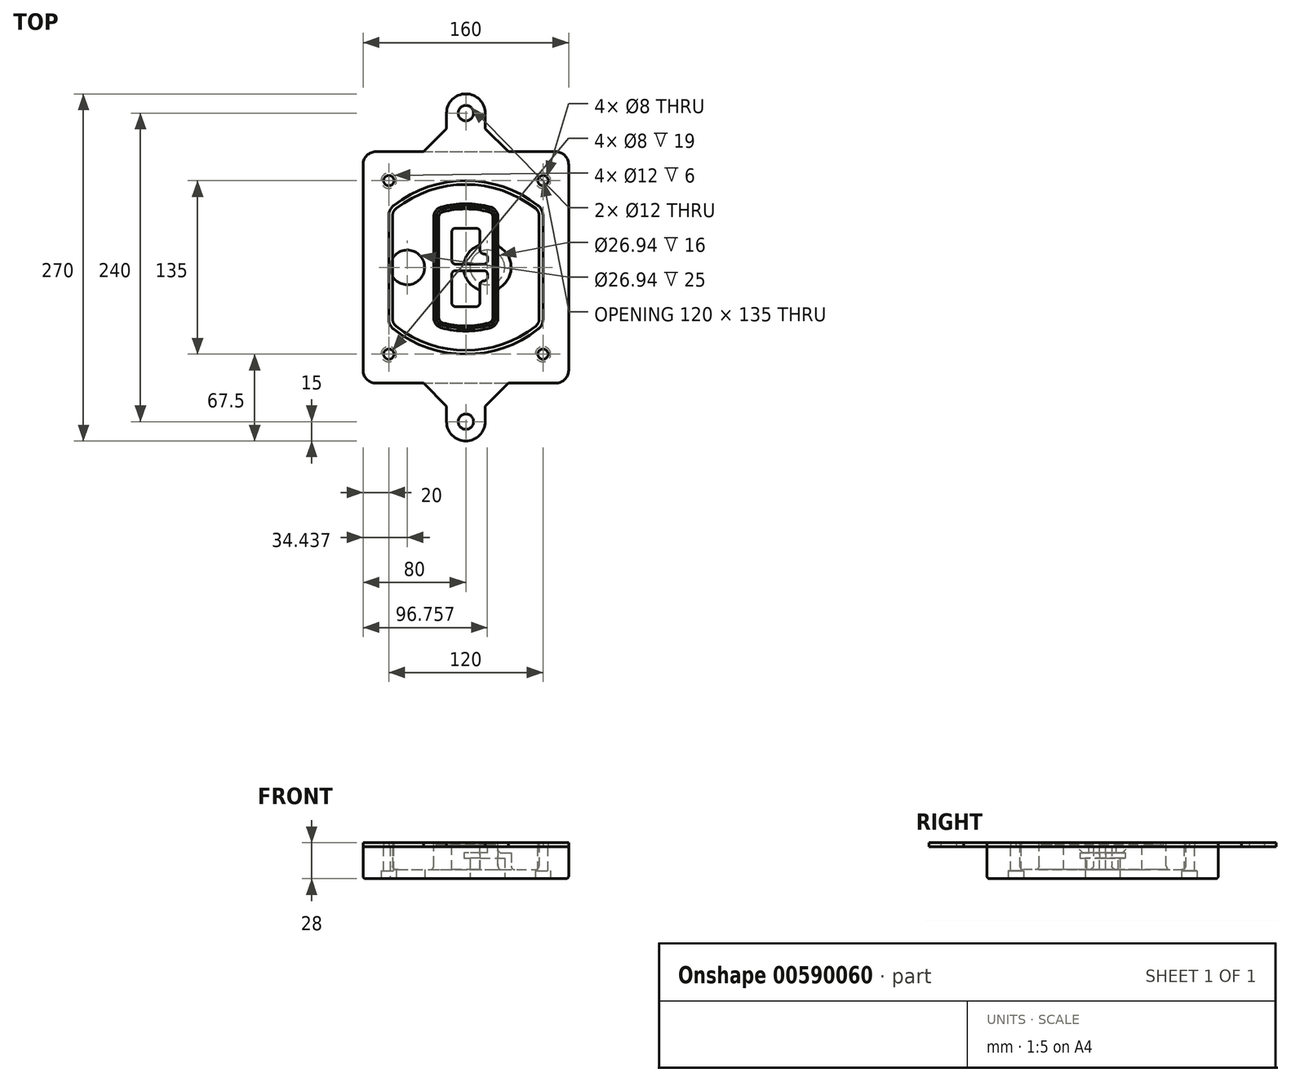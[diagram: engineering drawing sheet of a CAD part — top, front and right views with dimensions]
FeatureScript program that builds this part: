
annotation { "Feature Type Name" : "Feature", "Feature Type Description" : "" }
export const myFeature = defineFeature(function(context is Context, id is Id, definition is map)
    precondition{}
    {
        {
            var Q0;
            Q0=qCreatedBy(makeId("Top.planeOp"),FACE);
            var sketch = newSketch(context, id + "F0", { "sketchPlane" : qUnion([Q0])});
            skPoint(sketch, "E0.rect.middle", {"position": v(0, 0) * mm});
            skLineSegment(sketch, "E1.bottom", {"start": v(-70, -90) * mm, "end": v(70, -90) * mm});
            skLineSegment(sketch, "E1.top", {"start": v(-70, 90) * mm, "end": v(70, 90) * mm});
            skLineSegment(sketch, "E1.left", {"start": v(-80, -80) * mm, "end": v(-80, 80) * mm});
            skLineSegment(sketch, "E1.right", {"start": v(80, -80) * mm, "end": v(80, 80) * mm});
            skLineSegment(sketch, "E2", {"start": v(-80, 90) * mm, "end": v(80, -90) * mm, "construction": true});
            skLineSegment(sketch, "E3", {"start": v(80, 90) * mm, "end": v(-80, -90) * mm, "construction": true});
            skCircle(sketch, "E4", {"center": v(-60, 67.5) * mm, "radius": 4 * mm});
            skCircle(sketch, "E5", {"center": v(60, 67.5) * mm, "radius": 4 * mm});
            skCircle(sketch, "E6", {"center": v(60, -67.5) * mm, "radius": 4 * mm});
            skCircle(sketch, "E7", {"center": v(-60, -67.5) * mm, "radius": 4 * mm});
            skLineSegment(sketch, "E8", {"start": v(-60, 67.5) * mm, "end": v(60, 67.5) * mm, "construction": true});
            skLineSegment(sketch, "E9", {"start": v(60, 67.5) * mm, "end": v(60, -67.5) * mm, "construction": true});
            skLineSegment(sketch, "E10", {"start": v(60, -67.5) * mm, "end": v(-60, -67.5) * mm, "construction": true});
            skLineSegment(sketch, "E11", {"start": v(-60, -67.5) * mm, "end": v(-60, 67.5) * mm, "construction": true});
            skLineSegment(sketch, "E12", {"start": v(-60, 40.3) * mm, "end": v(-60, -40.3) * mm});
            skLineSegment(sketch, "E13", {"start": v(60, 40.3) * mm, "end": v(60, -40.3) * mm});
            skArc(sketch, "E14", {"start": v(56.15, 48.18) * mm, "mid": v(0, 67.5) * mm, "end": v(-56.15, 48.18) * mm});
            skArc(sketch, "E15", {"start": v(-56.15, -48.18) * mm, "mid": v(0, -67.5) * mm, "end": v(56.15, -48.18) * mm});
            skLineSegment(sketch, "E16", {"start": v(-60, 0) * mm, "end": v(60, 0) * mm, "construction": true});
            skPoint(sketch, "E17.visualSharp", {"position": v(-60, -45) * mm});
            skArc(sketch, "E17.filletArc", {"start": v(-60, -40.3) * mm, "mid": v(-58.99, -44.68) * mm, "end": v(-56.15, -48.18) * mm});
            skPoint(sketch, "E18.visualSharp", {"position": v(-60, 45) * mm});
            skArc(sketch, "E18.filletArc", {"start": v(-56.15, 48.18) * mm, "mid": v(-58.99, 44.68) * mm, "end": v(-60, 40.3) * mm});
            skPoint(sketch, "E19.visualSharp", {"position": v(60, 45) * mm});
            skArc(sketch, "E19.filletArc", {"start": v(60, 40.3) * mm, "mid": v(58.99, 44.68) * mm, "end": v(56.15, 48.18) * mm});
            skPoint(sketch, "E20.visualSharp", {"position": v(60, -45) * mm});
            skArc(sketch, "E20.filletArc", {"start": v(56.15, -48.18) * mm, "mid": v(58.99, -44.68) * mm, "end": v(60, -40.3) * mm});
            skPoint(sketch, "E21.visualSharp", {"position": v(-80, 90) * mm});
            skArc(sketch, "E21.filletArc", {"start": v(-70, 90) * mm, "mid": v(-77.07, 87.07) * mm, "end": v(-80, 80) * mm});
            skPoint(sketch, "E22.visualSharp", {"position": v(80, 90) * mm});
            skArc(sketch, "E22.filletArc", {"start": v(80, 80) * mm, "mid": v(77.07, 87.07) * mm, "end": v(70, 90) * mm});
            skPoint(sketch, "E23.visualSharp", {"position": v(80, -90) * mm});
            skArc(sketch, "E23.filletArc", {"start": v(70, -90) * mm, "mid": v(77.07, -87.07) * mm, "end": v(80, -80) * mm});
            skPoint(sketch, "E24.visualSharp", {"position": v(-80, -90) * mm});
            skArc(sketch, "E24.filletArc", {"start": v(-80, -80) * mm, "mid": v(-77.07, -87.07) * mm, "end": v(-70, -90) * mm});
            skArc(sketch, "E25.0", {"start": v(57, 40.3) * mm, "mid": v(56.3, 43.36) * mm, "end": v(54.3, 45.81) * mm});
            skLineSegment(sketch, "E25.1", {"start": v(57, 40.3) * mm, "end": v(57, -40.3) * mm});
            skArc(sketch, "E25.2", {"start": v(54.3, -45.81) * mm, "mid": v(56.3, -43.36) * mm, "end": v(57, -40.3) * mm});
            skArc(sketch, "E25.3", {"start": v(-54.3, -45.81) * mm, "mid": v(0, -64.5) * mm, "end": v(54.3, -45.81) * mm});
            skArc(sketch, "E25.4", {"start": v(-57, -40.3) * mm, "mid": v(-56.3, -43.36) * mm, "end": v(-54.3, -45.81) * mm});
            skArc(sketch, "E25.5", {"start": v(54.3, 45.81) * mm, "mid": v(0, 64.5) * mm, "end": v(-54.3, 45.81) * mm});
            skLineSegment(sketch, "E25.6", {"start": v(-57, 40.3) * mm, "end": v(-57, -40.3) * mm});
            skArc(sketch, "E25.7", {"start": v(-54.3, 45.81) * mm, "mid": v(-56.3, 43.36) * mm, "end": v(-57, 40.3) * mm});
            skArc(sketch, "E26.0", {"start": v(-58.62, 51.33) * mm, "mid": v(-62.58, 46.43) * mm, "end": v(-64, 40.3) * mm});
            skArc(sketch, "E26.1", {"start": v(58.62, 51.33) * mm, "mid": v(0, 71.5) * mm, "end": v(-58.62, 51.33) * mm});
            skArc(sketch, "E26.2", {"start": v(64, 40.3) * mm, "mid": v(62.58, 46.43) * mm, "end": v(58.62, 51.33) * mm});
            skLineSegment(sketch, "E26.3", {"start": v(64, 40.3) * mm, "end": v(64, -40.3) * mm});
            skArc(sketch, "E26.4", {"start": v(58.62, -51.33) * mm, "mid": v(62.58, -46.43) * mm, "end": v(64, -40.3) * mm});
            skLineSegment(sketch, "E26.5", {"start": v(-64, 40.3) * mm, "end": v(-64, -40.3) * mm});
            skArc(sketch, "E26.6", {"start": v(-58.62, -51.33) * mm, "mid": v(0, -71.5) * mm, "end": v(58.62, -51.33) * mm});
            skArc(sketch, "E26.7", {"start": v(-64, -40.3) * mm, "mid": v(-62.58, -46.43) * mm, "end": v(-58.62, -51.33) * mm});
            skSolve(sketch);
        }
        {
            var Q0;
            Q0=makeQuery(id+"F0.imprint","IMPRINT",FACE,{"disambiguationData":[TD([[makeQuery(id+"F0.imprint","IMPRINT",EDGE,{"derivedFrom":sQuery(id+"F0.wireOp",EDGE,"E1.bottom")}),1.0]])]});
            var Q1;
            Q1=makeQuery(id+"F0.imprint","IMPRINT",FACE,{"disambiguationData":[TD([[makeQuery(id+"F0.imprint","IMPRINT",EDGE,{"derivedFrom":sQuery(id+"F0.wireOp",EDGE,"E12")}),1.0]])]});
            var Q2;
            Q2=makeQuery(id+"F0.imprint","IMPRINT",FACE,{"disambiguationData":[TD([[makeQuery(id+"F0.imprint","IMPRINT",EDGE,{"derivedFrom":sQuery(id+"F0.wireOp",EDGE,"E25.0")}),1.0]])]});
            var Q3;
            Q3=makeQuery(id+"F0.imprint","IMPRINT",FACE,{"disambiguationData":[TD([[makeQuery(id+"F0.imprint","IMPRINT",EDGE,{"derivedFrom":sQuery(id+"F0.wireOp",EDGE,"E12")}),-1.0]])]});
            extrude(context, id + "F1", {"entities" : qUnion([Q0, Q1, Q2, Q3]), "oppositeDirection" : true, "depth" : 25 * mm});
        }
        {
            var Q0;
            Q0=makeQuery(id+"F0.imprint","IMPRINT",FACE,{"disambiguationData":[TD([[makeQuery(id+"F0.imprint","IMPRINT",EDGE,{"derivedFrom":sQuery(id+"F0.wireOp",EDGE,"E12")}),1.0]])]});
            extrude(context, id + "F2", {"entities" : qUnion([Q0]), "operationType" : NewBodyOperationType.ADD, "depth" : 3 * mm});
        }
        {
            var Q0;
            Q0=makeQuery(id+"F0.imprint","IMPRINT",FACE,{"disambiguationData":[TD([[makeQuery(id+"F0.imprint","IMPRINT",EDGE,{"derivedFrom":sQuery(id+"F0.wireOp",EDGE,"E25.0")}),1.0]])]});
            extrude(context, id + "F3", {"entities" : qUnion([Q0]), "operationType" : NewBodyOperationType.REMOVE, "oppositeDirection" : true, "depth" : 18 * mm});
        }
        {
            var Q0;
            Q0=makeQuery(id+"F2.opExtrude","CAP_FACE",FACE,{"disambiguationData":[OSD([sQuery(id+"F0.wireOp",EDGE,"E12"),sQuery(id+"F0.wireOp",EDGE,"E13"),sQuery(id+"F0.wireOp",EDGE,"E14"),sQuery(id+"F0.wireOp",EDGE,"E15"),sQuery(id+"F0.wireOp",EDGE,"E17.filletArc"),sQuery(id+"F0.wireOp",EDGE,"E18.filletArc"),sQuery(id+"F0.wireOp",EDGE,"E19.filletArc"),sQuery(id+"F0.wireOp",EDGE,"E20.filletArc"),sQuery(id+"F0.wireOp",EDGE,"E25.0"),sQuery(id+"F0.wireOp",EDGE,"E25.1"),sQuery(id+"F0.wireOp",EDGE,"E25.2"),sQuery(id+"F0.wireOp",EDGE,"E25.3"),sQuery(id+"F0.wireOp",EDGE,"E25.4"),sQuery(id+"F0.wireOp",EDGE,"E25.5"),sQuery(id+"F0.wireOp",EDGE,"E25.6"),sQuery(id+"F0.wireOp",EDGE,"E25.7")])],"isStart":false});
            var sketch = newSketch(context, id + "F4", { "sketchPlane" : qUnion([Q0])});
            skArc(sketch, "E27.0", {"start": v(-19.08, -46.97) * mm, "mid": v(0, -49.5) * mm, "end": v(19.08, -46.97) * mm});
            skArc(sketch, "E28.0", {"start": v(19.08, 46.97) * mm, "mid": v(0, 49.5) * mm, "end": v(-19.08, 46.97) * mm});
            skLineSegment(sketch, "E29", {"start": v(-25, 39.25) * mm, "end": v(-25, -39.25) * mm});
            skLineSegment(sketch, "E30", {"start": v(25, 39.25) * mm, "end": v(25, -39.25) * mm});
            skLineSegment(sketch, "E31", {"start": v(-25, 45.1) * mm, "end": v(25, 45.1) * mm, "construction": true});
            skLineSegment(sketch, "E32", {"start": v(-25, -45.1) * mm, "end": v(25, -45.1) * mm, "construction": true});
            skPoint(sketch, "E33.visualSharp", {"position": v(-25, 45.1) * mm});
            skArc(sketch, "E33.filletArc", {"start": v(-19.08, 46.97) * mm, "mid": v(-23.35, 44.11) * mm, "end": v(-25, 39.25) * mm});
            skPoint(sketch, "E34.visualSharp", {"position": v(25, 45.1) * mm});
            skArc(sketch, "E34.filletArc", {"start": v(25, 39.25) * mm, "mid": v(23.35, 44.11) * mm, "end": v(19.08, 46.97) * mm});
            skPoint(sketch, "E35.visualSharp", {"position": v(25, -45.1) * mm});
            skArc(sketch, "E35.filletArc", {"start": v(19.08, -46.97) * mm, "mid": v(23.35, -44.11) * mm, "end": v(25, -39.25) * mm});
            skPoint(sketch, "E36.visualSharp", {"position": v(-25, -45.1) * mm});
            skArc(sketch, "E36.filletArc", {"start": v(-25, -39.25) * mm, "mid": v(-23.35, -44.11) * mm, "end": v(-19.08, -46.97) * mm});
            skArc(sketch, "E37.0", {"start": v(54.3, 45.81) * mm, "mid": v(0, 64.5) * mm, "end": v(-54.3, 45.81) * mm});
            skArc(sketch, "E37.1", {"start": v(-54.3, 45.81) * mm, "mid": v(-56.3, 43.36) * mm, "end": v(-57, 40.3) * mm});
            skLineSegment(sketch, "E37.2", {"start": v(-57, 40.3) * mm, "end": v(-57, -40.3) * mm});
            skArc(sketch, "E37.3", {"start": v(-57, -40.3) * mm, "mid": v(-56.3, -43.36) * mm, "end": v(-54.3, -45.81) * mm});
            skArc(sketch, "E37.4", {"start": v(-54.3, -45.81) * mm, "mid": v(0, -64.5) * mm, "end": v(54.3, -45.81) * mm});
            skArc(sketch, "E37.5", {"start": v(54.3, -45.81) * mm, "mid": v(56.3, -43.36) * mm, "end": v(57, -40.3) * mm});
            skLineSegment(sketch, "E37.6", {"start": v(57, 40.3) * mm, "end": v(57, -40.3) * mm});
            skArc(sketch, "E37.7", {"start": v(57, 40.3) * mm, "mid": v(56.3, 43.36) * mm, "end": v(54.3, 45.81) * mm});
            skLineSegment(sketch, "E38.0", {"start": v(23, 39.25) * mm, "end": v(23, -39.25) * mm});
            skArc(sketch, "E38.1", {"start": v(18.56, -45.04) * mm, "mid": v(21.76, -42.9) * mm, "end": v(23, -39.25) * mm});
            skArc(sketch, "E38.2", {"start": v(-18.56, -45.04) * mm, "mid": v(0, -47.5) * mm, "end": v(18.56, -45.04) * mm});
            skArc(sketch, "E38.3", {"start": v(-23, -39.25) * mm, "mid": v(-21.76, -42.9) * mm, "end": v(-18.56, -45.04) * mm});
            skLineSegment(sketch, "E38.4", {"start": v(-23, 39.25) * mm, "end": v(-23, -39.25) * mm});
            skArc(sketch, "E38.5", {"start": v(23, 39.25) * mm, "mid": v(21.76, 42.9) * mm, "end": v(18.56, 45.04) * mm});
            skArc(sketch, "E38.6", {"start": v(-18.56, 45.04) * mm, "mid": v(-21.76, 42.9) * mm, "end": v(-23, 39.25) * mm});
            skArc(sketch, "E38.7", {"start": v(18.56, 45.04) * mm, "mid": v(0, 47.5) * mm, "end": v(-18.56, 45.04) * mm});
            skArc(sketch, "E39.0", {"start": v(21, 39.25) * mm, "mid": v(20.18, 41.68) * mm, "end": v(18.04, 43.1) * mm});
            skLineSegment(sketch, "E39.1", {"start": v(21, 39.25) * mm, "end": v(21, -39.25) * mm});
            skArc(sketch, "E39.2", {"start": v(18.04, -43.1) * mm, "mid": v(20.18, -41.68) * mm, "end": v(21, -39.25) * mm});
            skArc(sketch, "E39.3", {"start": v(-18.04, -43.1) * mm, "mid": v(0, -45.5) * mm, "end": v(18.04, -43.1) * mm});
            skArc(sketch, "E39.4", {"start": v(-21, -39.25) * mm, "mid": v(-20.18, -41.68) * mm, "end": v(-18.04, -43.1) * mm});
            skArc(sketch, "E39.5", {"start": v(18.04, 43.1) * mm, "mid": v(0, 45.5) * mm, "end": v(-18.04, 43.1) * mm});
            skLineSegment(sketch, "E39.6", {"start": v(-21, 39.25) * mm, "end": v(-21, -39.25) * mm});
            skArc(sketch, "E39.7", {"start": v(-18.04, 43.1) * mm, "mid": v(-20.18, 41.68) * mm, "end": v(-21, 39.25) * mm});
            skLineSegment(sketch, "E40", {"start": v(-25, 0) * mm, "end": v(25, 0) * mm, "construction": true});
            skLineSegment(sketch, "E41", {"start": v(-11, 5.5) * mm, "end": v(-11, 27.5) * mm});
            skLineSegment(sketch, "E42", {"start": v(-8, 30.5) * mm, "end": v(8, 30.5) * mm});
            skLineSegment(sketch, "E43", {"start": v(11, 27.5) * mm, "end": v(11, 13.5) * mm});
            skLineSegment(sketch, "E44", {"start": v(14, 10.5) * mm, "end": v(14, 10.5) * mm});
            skLineSegment(sketch, "E45", {"start": v(17, 7.5) * mm, "end": v(17, 5.5) * mm});
            skLineSegment(sketch, "E46", {"start": v(14, 2.5) * mm, "end": v(-8, 2.5) * mm});
            skPoint(sketch, "E47.visualSharp", {"position": v(-11, 30.5) * mm});
            skArc(sketch, "E47.filletArc", {"start": v(-8, 30.5) * mm, "mid": v(-10.12, 29.62) * mm, "end": v(-11, 27.5) * mm});
            skPoint(sketch, "E48.visualSharp", {"position": v(11, 30.5) * mm});
            skArc(sketch, "E48.filletArc", {"start": v(11, 27.5) * mm, "mid": v(10.12, 29.62) * mm, "end": v(8, 30.5) * mm});
            skPoint(sketch, "E49.visualSharp", {"position": v(11, 10.5) * mm});
            skArc(sketch, "E49.filletArc", {"start": v(11, 13.5) * mm, "mid": v(11.88, 11.38) * mm, "end": v(14, 10.5) * mm});
            skPoint(sketch, "E50.visualSharp", {"position": v(17, 10.5) * mm});
            skArc(sketch, "E50.filletArc", {"start": v(17, 7.5) * mm, "mid": v(16.12, 9.62) * mm, "end": v(14, 10.5) * mm});
            skPoint(sketch, "E51.visualSharp", {"position": v(17, 2.5) * mm});
            skArc(sketch, "E51.filletArc", {"start": v(14, 2.5) * mm, "mid": v(16.12, 3.38) * mm, "end": v(17, 5.5) * mm});
            skPoint(sketch, "E52.visualSharp", {"position": v(-11, 2.5) * mm});
            skArc(sketch, "E52.filletArc", {"start": v(-11, 5.5) * mm, "mid": v(-10.12, 3.38) * mm, "end": v(-8, 2.5) * mm});
            skLineSegment(sketch, "E53.0.MirrorCS", {"start": v(14, -2.5) * mm, "end": v(-8, -2.5) * mm});
            skArc(sketch, "E54.0.MirrorCS", {"start": v(-11, -5.5) * mm, "mid": v(-10.12, -3.38) * mm, "end": v(-8, -2.5) * mm});
            skLineSegment(sketch, "E55.0.MirrorCS", {"start": v(-11, -5.5) * mm, "end": v(-11, -27.5) * mm});
            skArc(sketch, "E56.0.MirrorCS", {"start": v(-8, -30.5) * mm, "mid": v(-10.12, -29.62) * mm, "end": v(-11, -27.5) * mm});
            skLineSegment(sketch, "E57.0.MirrorCS", {"start": v(-8, -30.5) * mm, "end": v(8, -30.5) * mm});
            skArc(sketch, "E58.0.MirrorCS", {"start": v(11, -27.5) * mm, "mid": v(10.12, -29.62) * mm, "end": v(8, -30.5) * mm});
            skLineSegment(sketch, "E59.0.MirrorCS", {"start": v(11, -27.5) * mm, "end": v(11, -13.5) * mm});
            skArc(sketch, "E60.0.MirrorCS", {"start": v(11, -13.5) * mm, "mid": v(11.88, -11.38) * mm, "end": v(14, -10.5) * mm});
            skArc(sketch, "E61.0.MirrorCS", {"start": v(17, -7.5) * mm, "mid": v(16.12, -9.62) * mm, "end": v(14, -10.5) * mm});
            skLineSegment(sketch, "E62.0.MirrorCS", {"start": v(17, -7.5) * mm, "end": v(17, -5.5) * mm});
            skArc(sketch, "E63.0.MirrorCS", {"start": v(14, -2.5) * mm, "mid": v(16.12, -3.38) * mm, "end": v(17, -5.5) * mm});
            skSolve(sketch);
        }
        {
            var Q0;
            Q0=makeQuery(id+"F4.imprint","IMPRINT",FACE,{"disambiguationData":[TD([[makeQuery(id+"F4.imprint","IMPRINT",EDGE,{"derivedFrom":sQuery(id+"F4.wireOp",EDGE,"E27.0")}),1.0]])]});
            var Q1;
            Q1=makeQuery(id+"F4.imprint","IMPRINT",FACE,{"disambiguationData":[TD([[makeQuery(id+"F4.imprint","IMPRINT",EDGE,{"derivedFrom":sQuery(id+"F4.wireOp",EDGE,"E38.0")}),-1.0]])]});
            var Q2;
            Q2=makeQuery(id+"F4.imprint","IMPRINT",FACE,{"disambiguationData":[TD([[makeQuery(id+"F4.imprint","IMPRINT",EDGE,{"derivedFrom":sQuery(id+"F4.wireOp",EDGE,"E39.0")}),1.0]])]});
            extrude(context, id + "F5", {"entities" : qUnion([Q0, Q1, Q2]), "operationType" : NewBodyOperationType.ADD, "endBound" : BoundingType.UP_TO_NEXT, "oppositeDirection" : true, "depth" : 25 * mm});
        }
        {
            var Q0;
            Q0=makeQuery(id+"F4.imprint","IMPRINT",FACE,{"disambiguationData":[TD([[makeQuery(id+"F4.imprint","IMPRINT",EDGE,{"derivedFrom":sQuery(id+"F4.wireOp",EDGE,"E38.0")}),-1.0]])]});
            extrude(context, id + "F6", {"entities" : qUnion([Q0]), "operationType" : NewBodyOperationType.REMOVE, "oppositeDirection" : true, "depth" : 2 * mm});
        }
        {
            var Q0;
            Q0=makeQuery(id+"F1.opExtrude","CAP_FACE",FACE,{"disambiguationData":[OSD([sQuery(id+"F0.wireOp",EDGE,"E1.bottom"),sQuery(id+"F0.wireOp",EDGE,"E1.top"),sQuery(id+"F0.wireOp",EDGE,"E1.left"),sQuery(id+"F0.wireOp",EDGE,"E1.right"),sQuery(id+"F0.wireOp",EDGE,"E4"),sQuery(id+"F0.wireOp",EDGE,"E5"),sQuery(id+"F0.wireOp",EDGE,"E6"),sQuery(id+"F0.wireOp",EDGE,"E7"),sQuery(id+"F0.wireOp",EDGE,"E21.filletArc"),sQuery(id+"F0.wireOp",EDGE,"E22.filletArc"),sQuery(id+"F0.wireOp",EDGE,"E23.filletArc"),sQuery(id+"F0.wireOp",EDGE,"E24.filletArc")])],"isStart":false});
            var sketch = newSketch(context, id + "F7", { "sketchPlane" : qUnion([Q0])});
            skCircle(sketch, "E64", {"center": v(16.76, 0) * mm, "radius": 13.47 * mm});
            skCircle(sketch, "E65", {"center": v(-45.56, 0) * mm, "radius": 13.47 * mm});
            skLineSegment(sketch, "E66", {"start": v(80, 0) * mm, "end": v(-80, 0) * mm});
            skCircle(sketch, "E67", {"center": v(16.76, 0) * mm, "radius": 18.47 * mm});
            skCircle(sketch, "E68", {"center": v(60, -67.5) * mm, "radius": 6 * mm});
            skCircle(sketch, "E69", {"center": v(-60, -67.5) * mm, "radius": 6 * mm});
            skCircle(sketch, "E70", {"center": v(-60, 67.5) * mm, "radius": 6 * mm});
            skCircle(sketch, "E71", {"center": v(60, 67.5) * mm, "radius": 6 * mm});
            skSolve(sketch);
        }
        {
            var Q0;
            {var subQ1=sQuery(id+"F7.wireOp",EDGE,"E66");var subQ4=sQuery(id+"F7.wireOp",EDGE,"E64");var subQ6=makeQuery(id+"F7.imprint","INTERSECT",VERTEX,{"disambiguationData":[OD(0.0)],"derivedFrom":[subQ4,subQ1]});Q0=makeQuery(id+"F7.imprint","IMPRINT",FACE,{"disambiguationData":[TD([[makeQuery(id+"F7.imprint","IMPRINT",EDGE,{"disambiguationData":[TD([[subQ6,-1.0]])],"derivedFrom":subQ4}),-1.0]])]});}
            var Q1;
            {var subQ0=sQuery(id+"F7.wireOp",EDGE,"E66");var subQ1=sQuery(id+"F7.wireOp",EDGE,"E64");var subQ3=makeQuery(id+"F7.imprint","INTERSECT",VERTEX,{"disambiguationData":[OD(0.0)],"derivedFrom":[subQ1,subQ0]});Q1=makeQuery(id+"F7.imprint","IMPRINT",FACE,{"disambiguationData":[TD([[makeQuery(id+"F7.imprint","IMPRINT",EDGE,{"disambiguationData":[TD([[subQ3,-1.0]])],"derivedFrom":subQ1}),1.0]])]});}
            var Q2;
            {var subQ0=sQuery(id+"F7.wireOp",EDGE,"E66");var subQ1=sQuery(id+"F7.wireOp",EDGE,"E64");var subQ3=makeQuery(id+"F7.imprint","INTERSECT",VERTEX,{"disambiguationData":[OD(0.0)],"derivedFrom":[subQ1,subQ0]});Q2=makeQuery(id+"F7.imprint","IMPRINT",FACE,{"disambiguationData":[TD([[makeQuery(id+"F7.imprint","IMPRINT",EDGE,{"disambiguationData":[TD([[subQ3,1.0]])],"derivedFrom":subQ1}),1.0]])]});}
            var Q3;
            {var subQ1=sQuery(id+"F7.wireOp",EDGE,"E66");var subQ4=sQuery(id+"F7.wireOp",EDGE,"E64");var subQ6=makeQuery(id+"F7.imprint","INTERSECT",VERTEX,{"disambiguationData":[OD(0.0)],"derivedFrom":[subQ4,subQ1]});Q3=makeQuery(id+"F7.imprint","IMPRINT",FACE,{"disambiguationData":[TD([[makeQuery(id+"F7.imprint","IMPRINT",EDGE,{"disambiguationData":[TD([[subQ6,1.0]])],"derivedFrom":subQ4}),-1.0]])]});}
            extrude(context, id + "F8", {"entities" : qUnion([Q0, Q1, Q2, Q3]), "operationType" : NewBodyOperationType.ADD, "oppositeDirection" : true, "depth" : 20 * mm});
        }
        {
            var Q0;
            {var subQ0=sQuery(id+"F7.wireOp",EDGE,"E66");var subQ1=sQuery(id+"F7.wireOp",EDGE,"E64");var subQ3=makeQuery(id+"F7.imprint","INTERSECT",VERTEX,{"disambiguationData":[OD(0.0)],"derivedFrom":[subQ1,subQ0]});Q0=makeQuery(id+"F7.imprint","IMPRINT",FACE,{"disambiguationData":[TD([[makeQuery(id+"F7.imprint","IMPRINT",EDGE,{"disambiguationData":[TD([[subQ3,-1.0]])],"derivedFrom":subQ1}),1.0]])]});}
            var Q1;
            {var subQ0=sQuery(id+"F7.wireOp",EDGE,"E66");var subQ1=sQuery(id+"F7.wireOp",EDGE,"E64");var subQ3=makeQuery(id+"F7.imprint","INTERSECT",VERTEX,{"disambiguationData":[OD(0.0)],"derivedFrom":[subQ1,subQ0]});Q1=makeQuery(id+"F7.imprint","IMPRINT",FACE,{"disambiguationData":[TD([[makeQuery(id+"F7.imprint","IMPRINT",EDGE,{"disambiguationData":[TD([[subQ3,1.0]])],"derivedFrom":subQ1}),1.0]])]});}
            extrude(context, id + "F9", {"entities" : qUnion([Q0, Q1]), "operationType" : NewBodyOperationType.REMOVE, "oppositeDirection" : true, "depth" : 16 * mm});
        }
        {
            var Q0;
            {var subQ0=sQuery(id+"F7.wireOp",EDGE,"E66");var subQ1=sQuery(id+"F7.wireOp",EDGE,"E65");var subQ3=makeQuery(id+"F7.imprint","INTERSECT",VERTEX,{"disambiguationData":[OD(0.0)],"derivedFrom":[subQ1,subQ0]});Q0=makeQuery(id+"F7.imprint","IMPRINT",FACE,{"disambiguationData":[TD([[makeQuery(id+"F7.imprint","IMPRINT",EDGE,{"disambiguationData":[TD([[subQ3,-1.0]])],"derivedFrom":subQ1}),1.0]])]});}
            var Q1;
            {var subQ0=sQuery(id+"F7.wireOp",EDGE,"E66");var subQ1=sQuery(id+"F7.wireOp",EDGE,"E65");var subQ3=makeQuery(id+"F7.imprint","INTERSECT",VERTEX,{"disambiguationData":[OD(0.0)],"derivedFrom":[subQ1,subQ0]});Q1=makeQuery(id+"F7.imprint","IMPRINT",FACE,{"disambiguationData":[TD([[makeQuery(id+"F7.imprint","IMPRINT",EDGE,{"disambiguationData":[TD([[subQ3,1.0]])],"derivedFrom":subQ1}),1.0]])]});}
            extrude(context, id + "F10", {"entities" : qUnion([Q0, Q1]), "operationType" : NewBodyOperationType.REMOVE, "oppositeDirection" : true, "depth" : 25 * mm});
        }
        {
            var Q0;
            Q0=makeQuery(id+"F7.imprint","IMPRINT",FACE,{"disambiguationData":[TD([[makeQuery(id+"F7.imprint","IMPRINT",EDGE,{"derivedFrom":sQuery(id+"F7.wireOp",EDGE,"E68")}),1.0]])]});
            var Q1;
            Q1=makeQuery(id+"F7.imprint","IMPRINT",FACE,{"disambiguationData":[TD([[makeQuery(id+"F7.imprint","IMPRINT",EDGE,{"derivedFrom":makeQuery(id+"F1.opExtrude","CAP_EDGE",EDGE,{"disambiguationData":[OSD([sQuery(id+"F0.wireOp",EDGE,"E5")])],"isStart":false})}),-1.0]])]});
            var Q2;
            Q2=makeQuery(id+"F7.imprint","IMPRINT",FACE,{"disambiguationData":[TD([[makeQuery(id+"F7.imprint","IMPRINT",EDGE,{"derivedFrom":sQuery(id+"F7.wireOp",EDGE,"E69")}),1.0]])]});
            var Q3;
            Q3=makeQuery(id+"F7.imprint","IMPRINT",FACE,{"disambiguationData":[TD([[makeQuery(id+"F7.imprint","IMPRINT",EDGE,{"derivedFrom":makeQuery(id+"F1.opExtrude","CAP_EDGE",EDGE,{"disambiguationData":[OSD([sQuery(id+"F0.wireOp",EDGE,"E4")])],"isStart":false})}),-1.0]])]});
            var Q4;
            Q4=makeQuery(id+"F7.imprint","IMPRINT",FACE,{"disambiguationData":[TD([[makeQuery(id+"F7.imprint","IMPRINT",EDGE,{"derivedFrom":sQuery(id+"F7.wireOp",EDGE,"E70")}),1.0]])]});
            var Q5;
            Q5=makeQuery(id+"F7.imprint","IMPRINT",FACE,{"disambiguationData":[TD([[makeQuery(id+"F7.imprint","IMPRINT",EDGE,{"derivedFrom":makeQuery(id+"F1.opExtrude","CAP_EDGE",EDGE,{"disambiguationData":[OSD([sQuery(id+"F0.wireOp",EDGE,"E7")])],"isStart":false})}),-1.0]])]});
            var Q6;
            Q6=makeQuery(id+"F7.imprint","IMPRINT",FACE,{"disambiguationData":[TD([[makeQuery(id+"F7.imprint","IMPRINT",EDGE,{"derivedFrom":sQuery(id+"F7.wireOp",EDGE,"E71")}),1.0]])]});
            var Q7;
            Q7=makeQuery(id+"F7.imprint","IMPRINT",FACE,{"disambiguationData":[TD([[makeQuery(id+"F7.imprint","IMPRINT",EDGE,{"derivedFrom":makeQuery(id+"F1.opExtrude","CAP_EDGE",EDGE,{"disambiguationData":[OSD([sQuery(id+"F0.wireOp",EDGE,"E6")])],"isStart":false})}),-1.0]])]});
            extrude(context, id + "F11", {"entities" : qUnion([Q0, Q1, Q2, Q3, Q4, Q5, Q6, Q7]), "operationType" : NewBodyOperationType.REMOVE, "oppositeDirection" : true, "depth" : 6 * mm});
        }
        {
            var Q0;
            Q0=makeQuery(id+"F9.boolean.opBoolean","COPY",FACE,{"derivedFrom":makeQuery(id+"F9.opExtrude","CAP_FACE",FACE,{"disambiguationData":[OSD([sQuery(id+"F7.wireOp",EDGE,"E64")])],"isStart":false})});
            var sketch = newSketch(context, id + "F12", { "sketchPlane" : qUnion([Q0])});
            skArc(sketch, "E72.0", {"start": v(11, 17.55) * mm, "mid": v(2.57, 11.82) * mm, "end": v(-1.54, 2.5) * mm});
            skArc(sketch, "E72.1", {"start": v(-1.54, -2.5) * mm, "mid": v(2.57, -11.82) * mm, "end": v(11, -17.55) * mm});
            skLineSegment(sketch, "E73", {"start": v(-1.54, -2.5) * mm, "end": v(14, -2.5) * mm});
            skLineSegment(sketch, "E74.0", {"start": v(14, 2.5) * mm, "end": v(-1.54, 2.5) * mm});
            skArc(sketch, "E74.1", {"start": v(14, 2.5) * mm, "mid": v(16.12, 3.38) * mm, "end": v(17, 5.5) * mm});
            skLineSegment(sketch, "E74.2", {"start": v(17, 7.5) * mm, "end": v(17, 5.5) * mm});
            skArc(sketch, "E74.3", {"start": v(17, 7.5) * mm, "mid": v(16.12, 9.62) * mm, "end": v(14, 10.5) * mm});
            skArc(sketch, "E74.4", {"start": v(11, 13.5) * mm, "mid": v(11.88, 11.38) * mm, "end": v(14, 10.5) * mm});
            skLineSegment(sketch, "E74.5", {"start": v(11, 17.55) * mm, "end": v(11, 13.5) * mm});
            skLineSegment(sketch, "E74.7", {"start": v(14, -2.5) * mm, "end": v(-1.54, -2.5) * mm});
            skArc(sketch, "E74.8", {"start": v(14, -2.5) * mm, "mid": v(16.12, -3.38) * mm, "end": v(17, -5.5) * mm});
            skLineSegment(sketch, "E74.9", {"start": v(17, -7.5) * mm, "end": v(17, -5.5) * mm});
            skArc(sketch, "E74.10", {"start": v(17, -7.5) * mm, "mid": v(16.12, -9.62) * mm, "end": v(14, -10.5) * mm});
            skArc(sketch, "E74.11", {"start": v(11, -13.5) * mm, "mid": v(11.88, -11.38) * mm, "end": v(14, -10.5) * mm});
            skLineSegment(sketch, "E74.12", {"start": v(11, -17.55) * mm, "end": v(11, -13.5) * mm});
            skPoint(sketch, "E75.orphan", {"position": v(11, -27.5) * mm});
            skPoint(sketch, "E76.orphan", {"position": v(-8, -2.5) * mm});
            skPoint(sketch, "E77.orphan", {"position": v(-8, 2.5) * mm});
            skPoint(sketch, "E78.orphan", {"position": v(11, 27.5) * mm});
            skSolve(sketch);
        }
        {
            var Q0;
            {var subQ7=sQuery(id+"F12.wireOp",EDGE,"E72.0");var subQ14=sQuery(id+"F12.wireOp",EDGE,"E72.1");var subQ16=sQuery(id+"F12.wireOp",EDGE,"E74.1");var subQ18=sQuery(id+"F12.wireOp",EDGE,"E74.8");Q0=qUnion([makeQuery(id+"F12.imprint","IMPRINT",FACE,{"disambiguationData":[TD([[makeQuery(id+"F12.imprint","IMPRINT",EDGE,{"derivedFrom":subQ7}),1.0]])]}),makeQuery(id+"F12.imprint","IMPRINT",FACE,{"disambiguationData":[TD([[makeQuery(id+"F12.imprint","IMPRINT",EDGE,{"derivedFrom":subQ14}),1.0]])]}),makeQuery(id+"F12.imprint","IMPRINT",FACE,{"disambiguationData":[TD([[makeQuery(id+"F12.imprint","IMPRINT",EDGE,{"derivedFrom":subQ16}),1.0]])]}),makeQuery(id+"F12.imprint","IMPRINT",FACE,{"disambiguationData":[TD([[makeQuery(id+"F12.imprint","IMPRINT",EDGE,{"derivedFrom":subQ18}),-1.0]])]})]);}
            var Q1;
            Q1=makeQuery(id+"F5.boolean.opBoolean","SPLIT",FACE,{"disambiguationData":[TD([makeQuery(id+"F5.opExtrude","SWEPT_FACE",FACE,{"disambiguationData":[OSD([sQuery(id+"F4.wireOp",EDGE,"E41")])]})])],"derivedFrom":makeQuery(id+"F3.boolean.opBoolean","COPY",FACE,{"derivedFrom":makeQuery(id+"F3.opExtrude","CAP_FACE",FACE,{"disambiguationData":[OSD([sQuery(id+"F0.wireOp",EDGE,"E25.0"),sQuery(id+"F0.wireOp",EDGE,"E25.1"),sQuery(id+"F0.wireOp",EDGE,"E25.2"),sQuery(id+"F0.wireOp",EDGE,"E25.3"),sQuery(id+"F0.wireOp",EDGE,"E25.4"),sQuery(id+"F0.wireOp",EDGE,"E25.5"),sQuery(id+"F0.wireOp",EDGE,"E25.6"),sQuery(id+"F0.wireOp",EDGE,"E25.7")])],"isStart":false})})});
            extrude(context, id + "F13", {"entities" : qUnion([Q0]), "operationType" : NewBodyOperationType.REMOVE, "endBound" : BoundingType.UP_TO_SURFACE, "endBoundEntityFace" : qUnion([Q1]), "depth" : 25 * mm});
        }
        {
            var Q0;
            Q0=makeQuery(id+"F3.boolean.opBoolean","COPY",EDGE,{"derivedFrom":makeQuery(id+"F3.opExtrude","CAP_EDGE",EDGE,{"disambiguationData":[OSD([sQuery(id+"F0.wireOp",EDGE,"E25.6")])],"isStart":false})});
            var Q1;
            Q1=makeQuery(id+"F8.boolean.opBoolean","INTERSECT",EDGE,{"derivedFrom":[makeQuery(id+"F5.opExtrude","SWEPT_FACE",FACE,{"disambiguationData":[OSD([sQuery(id+"F4.wireOp",EDGE,"E30")])]}),makeQuery(id+"F8.opExtrude","CAP_FACE",FACE,{"disambiguationData":[OSD([sQuery(id+"F7.wireOp",EDGE,"E67")])],"isStart":false})]});
            var Q2;
            Q2=makeQuery(id+"F8.boolean.opBoolean","INTERSECT",EDGE,{"disambiguationData":[OD(1.0)],"derivedFrom":[makeQuery(id+"F5.opExtrude","SWEPT_FACE",FACE,{"disambiguationData":[OSD([sQuery(id+"F4.wireOp",EDGE,"E30")])]}),makeQuery(id+"F8.opExtrude","SWEPT_FACE",FACE,{"disambiguationData":[OSD([sQuery(id+"F7.wireOp",EDGE,"E67")])]})]});
            var Q3;
            {var subQ0=sQuery(id+"F4.wireOp",EDGE,"E30");Q3=makeQuery(id+"F8.boolean.opBoolean","SPLIT",EDGE,{"disambiguationData":[TD([makeQuery(id+"F5.opExtrude","SWEPT_FACE",FACE,{"disambiguationData":[OSD([sQuery(id+"F4.wireOp",EDGE,"E35.filletArc")])]})])],"derivedFrom":makeQuery(id+"F5.opExtrude","CAP_EDGE",EDGE,{"disambiguationData":[OSD([subQ0])],"isStart":false})});}
            var Q4;
            {var subQ0=sQuery(id+"F0.wireOp",EDGE,"E25.7");var subQ1=sQuery(id+"F0.wireOp",EDGE,"E25.1");var subQ2=sQuery(id+"F0.wireOp",EDGE,"E25.6");var subQ3=sQuery(id+"F0.wireOp",EDGE,"E25.5");var subQ4=sQuery(id+"F0.wireOp",EDGE,"E25.4");var subQ5=sQuery(id+"F0.wireOp",EDGE,"E25.0");var subQ6=sQuery(id+"F0.wireOp",EDGE,"E25.2");var subQ7=sQuery(id+"F0.wireOp",EDGE,"E25.3");Q4=makeQuery(id+"F8.boolean.opBoolean","INTERSECT",EDGE,{"derivedFrom":[makeQuery(id+"F5.boolean.opBoolean","SPLIT",FACE,{"disambiguationData":[TD([makeQuery(id+"F2.opExtrude","SWEPT_FACE",FACE,{"disambiguationData":[OSD([subQ5])]})])],"derivedFrom":makeQuery(id+"F3.boolean.opBoolean","COPY",FACE,{"derivedFrom":makeQuery(id+"F3.opExtrude","CAP_FACE",FACE,{"disambiguationData":[OSD([subQ5,subQ1,subQ6,subQ7,subQ4,subQ3,subQ2,subQ0])],"isStart":false})})}),makeQuery(id+"F8.opExtrude","SWEPT_FACE",FACE,{"disambiguationData":[OSD([sQuery(id+"F7.wireOp",EDGE,"E67")])]})]});}
            var Q5;
            Q5=makeQuery(id+"F8.boolean.opBoolean","INTERSECT",EDGE,{"disambiguationData":[OD(0.0)],"derivedFrom":[makeQuery(id+"F5.opExtrude","SWEPT_FACE",FACE,{"disambiguationData":[OSD([sQuery(id+"F4.wireOp",EDGE,"E30")])]}),makeQuery(id+"F8.opExtrude","SWEPT_FACE",FACE,{"disambiguationData":[OSD([sQuery(id+"F7.wireOp",EDGE,"E67")])]})]});
            fillet(context, id + "F14", {"entities" : qUnion([Q0, Q1, Q2, Q3, Q4, Q5]), "radius" : 3 * mm, "tangentPropagation" : true, "allowEdgeOverflow" : false});
        }
        {
            var Q0;
            Q0=makeQuery(id+"F1.opExtrude","CAP_EDGE",EDGE,{"disambiguationData":[OSD([sQuery(id+"F0.wireOp",EDGE,"E1.bottom")])],"isStart":false});
            fillet(context, id + "F15", {"entities" : qUnion([Q0]), "radius" : 2 * mm, "tangentPropagation" : true, "allowEdgeOverflow" : false});
        }
        {
            var Q0;
            {var subQ0=sQuery(id+"F0.wireOp",EDGE,"E21.filletArc");var subQ1=sQuery(id+"F0.wireOp",EDGE,"E7");var subQ2=sQuery(id+"F0.wireOp",EDGE,"E6");var subQ3=sQuery(id+"F0.wireOp",EDGE,"E5");var subQ4=sQuery(id+"F0.wireOp",EDGE,"E4");var subQ5=sQuery(id+"F0.wireOp",EDGE,"E22.filletArc");var subQ6=sQuery(id+"F0.wireOp",EDGE,"E1.bottom");var subQ7=sQuery(id+"F0.wireOp",EDGE,"E1.right");var subQ8=sQuery(id+"F0.wireOp",EDGE,"E1.top");var subQ9=sQuery(id+"F0.wireOp",EDGE,"E1.left");var subQ10=sQuery(id+"F0.wireOp",EDGE,"E23.filletArc");var subQ11=sQuery(id+"F0.wireOp",EDGE,"E24.filletArc");Q0=makeQuery(id+"F2.boolean.opBoolean","SPLIT",FACE,{"disambiguationData":[TD([makeQuery(id+"F1.opExtrude","SWEPT_FACE",FACE,{"disambiguationData":[OSD([subQ6])]})])],"derivedFrom":makeQuery(id+"F1.opExtrude","CAP_FACE",FACE,{"disambiguationData":[OSD([subQ6,subQ8,subQ9,subQ7,subQ4,subQ3,subQ2,subQ1,subQ0,subQ5,subQ10,subQ11])],"isStart":true})});}
            var sketch = newSketch(context, id + "F16", { "sketchPlane" : qUnion([Q0])});
            skLineSegment(sketch, "E79.0", {"start": v(-70, 90) * mm, "end": v(70, 90) * mm});
            skArc(sketch, "E80.0", {"start": v(-70, 90) * mm, "mid": v(-77.07, 87.07) * mm, "end": v(-80, 80) * mm});
            skLineSegment(sketch, "E80.1", {"start": v(-80, -80) * mm, "end": v(-80, 80) * mm});
            skArc(sketch, "E80.2", {"start": v(-80, -80) * mm, "mid": v(-77.07, -87.07) * mm, "end": v(-70, -90) * mm});
            skArc(sketch, "E80.4", {"start": v(70, -90) * mm, "mid": v(77.07, -87.07) * mm, "end": v(80, -80) * mm});
            skLineSegment(sketch, "E80.5", {"start": v(80, -80) * mm, "end": v(80, 80) * mm});
            skArc(sketch, "E80.6", {"start": v(80, 80) * mm, "mid": v(77.07, 87.07) * mm, "end": v(70, 90) * mm});
            skCircle(sketch, "E80.9", {"center": v(-60, -67.5) * mm, "radius": 4 * mm});
            skCircle(sketch, "E80.10", {"center": v(60, -67.5) * mm, "radius": 4 * mm});
            skCircle(sketch, "E80.12", {"center": v(60, 67.5) * mm, "radius": 4 * mm});
            skPoint(sketch, "E80.13", {"position": v(77.07, -87.07) * mm});
            skPoint(sketch, "E80.14", {"position": v(77.07, 87.07) * mm});
            skCircle(sketch, "E81.0", {"center": v(-60, 67.5) * mm, "radius": 4 * mm});
            skArc(sketch, "E82.0", {"start": v(56.15, 48.18) * mm, "mid": v(0, 67.5) * mm, "end": v(-56.15, 48.18) * mm});
            skArc(sketch, "E82.1", {"start": v(-56.15, 48.18) * mm, "mid": v(-58.99, 44.68) * mm, "end": v(-60, 40.3) * mm});
            skLineSegment(sketch, "E82.2", {"start": v(-60, 40.3) * mm, "end": v(-60, -40.3) * mm});
            skArc(sketch, "E82.3", {"start": v(-56.15, -48.18) * mm, "mid": v(0, -67.5) * mm, "end": v(56.15, -48.18) * mm});
            skArc(sketch, "E82.4", {"start": v(-60, -40.3) * mm, "mid": v(-58.99, -44.68) * mm, "end": v(-56.15, -48.18) * mm});
            skArc(sketch, "E82.5", {"start": v(56.15, -48.18) * mm, "mid": v(58.99, -44.68) * mm, "end": v(60, -40.3) * mm});
            skLineSegment(sketch, "E82.6", {"start": v(60, 40.3) * mm, "end": v(60, -40.3) * mm});
            skArc(sketch, "E82.7", {"start": v(60, 40.3) * mm, "mid": v(58.99, 44.68) * mm, "end": v(56.15, 48.18) * mm});
            skLineSegment(sketch, "E83", {"start": v(0, 90) * mm, "end": v(0, 120) * mm, "construction": true});
            skCircle(sketch, "E84", {"center": v(0, 120) * mm, "radius": 6 * mm});
            skArc(sketch, "E85", {"start": v(-15, 120) * mm, "mid": v(0, 135) * mm, "end": v(15, 120) * mm});
            skLineSegment(sketch, "E86", {"start": v(-15, 120) * mm, "end": v(-15, 108) * mm});
            skLineSegment(sketch, "E87", {"start": v(15, 120) * mm, "end": v(15, 108) * mm});
            skLineSegment(sketch, "E88", {"start": v(15, 108) * mm, "end": v(33, 90) * mm});
            skLineSegment(sketch, "E89", {"start": v(-15, 108) * mm, "end": v(-33, 90) * mm});
            skArc(sketch, "E90.MirrorCS", {"start": v(15, 120) * mm, "mid": v(0, 135) * mm, "end": v(-15, 120) * mm});
            skLineSegment(sketch, "E91.MirrorCS", {"start": v(70, 90) * mm, "end": v(-70, 90) * mm});
            skLineSegment(sketch, "E92", {"start": v(-80, 0) * mm, "end": v(80, 0) * mm, "construction": true});
            skLineSegment(sketch, "E93.MirrorCS", {"start": v(-15, -120) * mm, "end": v(-15, -108) * mm});
            skLineSegment(sketch, "E94.MirrorCS", {"start": v(15, -120) * mm, "end": v(15, -108) * mm});
            skArc(sketch, "E95.MirrorCS", {"start": v(-15, -120) * mm, "mid": v(0, -135) * mm, "end": v(15, -120) * mm});
            skArc(sketch, "E96.MirrorCS", {"start": v(15, -120) * mm, "mid": v(0, -135) * mm, "end": v(-15, -120) * mm});
            skLineSegment(sketch, "E97.MirrorCS", {"start": v(-15, -108) * mm, "end": v(-33, -90) * mm});
            skCircle(sketch, "E98.MirrorC", {"center": v(0, -120) * mm, "radius": 6 * mm});
            skLineSegment(sketch, "E99.MirrorCS", {"start": v(15, -108) * mm, "end": v(33, -90) * mm});
            skLineSegment(sketch, "E100.MirrorCS", {"start": v(70, -90) * mm, "end": v(-70, -90) * mm});
            skLineSegment(sketch, "E101.MirrorCS", {"start": v(0, -90) * mm, "end": v(0, -120) * mm, "construction": true});
            skSolve(sketch);
        }
        {
            var Q0;
            Q0 = qSketchRegion(id + "F16", true);
            var Q1;
            Q1=makeQuery(id+"F2.opExtrude","CAP_FACE",FACE,{"disambiguationData":[OSD([sQuery(id+"F0.wireOp",EDGE,"E12"),sQuery(id+"F0.wireOp",EDGE,"E13"),sQuery(id+"F0.wireOp",EDGE,"E14"),sQuery(id+"F0.wireOp",EDGE,"E15"),sQuery(id+"F0.wireOp",EDGE,"E17.filletArc"),sQuery(id+"F0.wireOp",EDGE,"E18.filletArc"),sQuery(id+"F0.wireOp",EDGE,"E19.filletArc"),sQuery(id+"F0.wireOp",EDGE,"E20.filletArc"),sQuery(id+"F0.wireOp",EDGE,"E25.0"),sQuery(id+"F0.wireOp",EDGE,"E25.1"),sQuery(id+"F0.wireOp",EDGE,"E25.2"),sQuery(id+"F0.wireOp",EDGE,"E25.3"),sQuery(id+"F0.wireOp",EDGE,"E25.4"),sQuery(id+"F0.wireOp",EDGE,"E25.5"),sQuery(id+"F0.wireOp",EDGE,"E25.6"),sQuery(id+"F0.wireOp",EDGE,"E25.7")])],"isStart":false});
            extrude(context, id + "F17", {"entities" : qUnion([Q0]), "endBound" : BoundingType.UP_TO_SURFACE, "depth" : 25 * mm, "endBoundEntityFace" : qUnion([Q1]), "offsetDistance" : 25 * mm});
        }
    });
